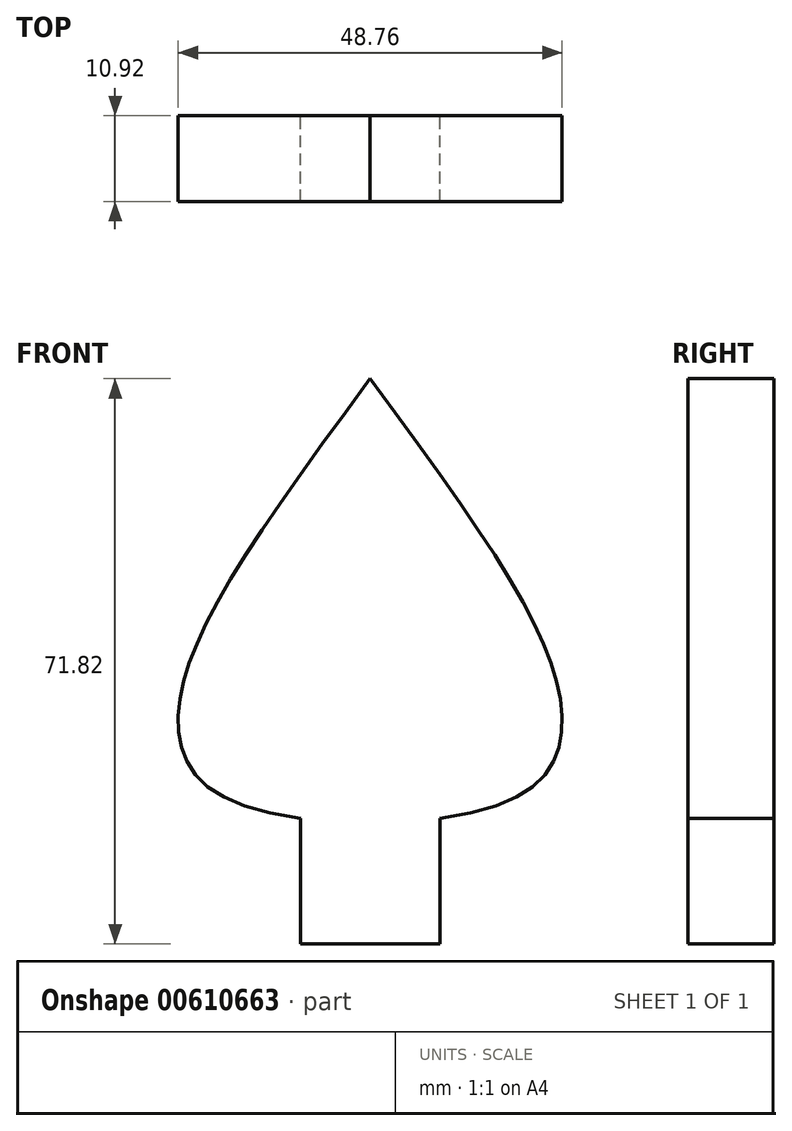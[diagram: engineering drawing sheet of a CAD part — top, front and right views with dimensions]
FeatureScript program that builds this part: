
annotation { "Feature Type Name" : "Feature", "Feature Type Description" : "" }
export const myFeature = defineFeature(function(context is Context, id is Id, definition is map)
    precondition{}
    {
        {
            var Q0;
            Q0=qCreatedBy(makeId("Front.planeOp"),FACE);
            var sketch = newSketch(context, id + "F0", { "sketchPlane" : qUnion([Q0])});
            skFitSpline(sketch, "E0", {"points": [v(0, 0) * mm, v(24.38, 13.06) * mm, v(0, 56.32) * mm], "startDerivative": vector(138.94, 0) * mm, "endDerivative": vector(-80.61, 109.32) * mm});
            skFitSpline(sketch, "E1.MirrorCS", {"points": [v(0, 0) * mm, v(-24.38, 13.06) * mm, v(0, 56.32) * mm], "startDerivative": vector(-138.94, 0) * mm, "endDerivative": vector(80.61, 109.32) * mm});
            skLineSegment(sketch, "E2.bottom", {"start": v(-8.84, -15.5) * mm, "end": v(8.84, -15.5) * mm});
            skLineSegment(sketch, "E2.left", {"start": v(-8.84, -15.5) * mm, "end": v(-8.84, 0.48) * mm});
            skLineSegment(sketch, "E2.right", {"start": v(8.84, -15.5) * mm, "end": v(8.84, 0.48) * mm});
            skSolve(sketch);
        }
        {
            var Q0;
            Q0 = qSketchRegion(id + "F0", true);
            extrude(context, id + "F1", {"entities" : qUnion([Q0]), "depth" : 10.92 * mm, "offsetDistance" : 25.4 * mm});
        }
    });
